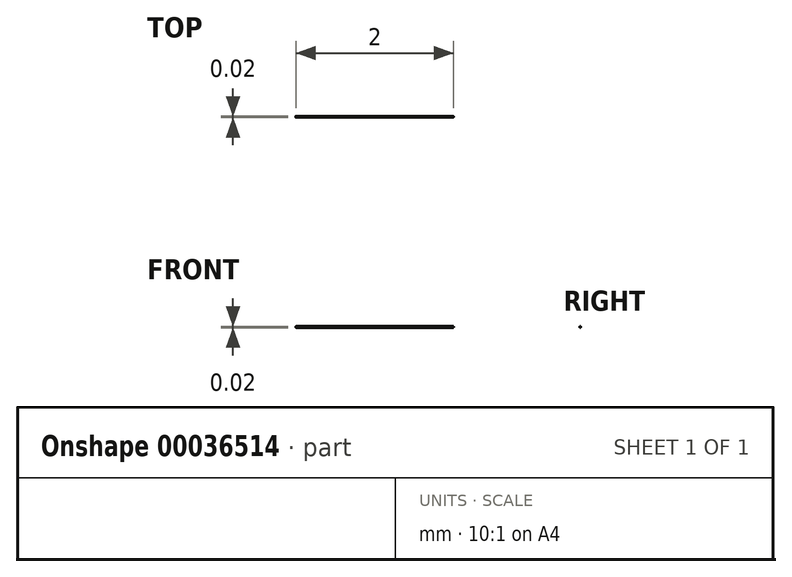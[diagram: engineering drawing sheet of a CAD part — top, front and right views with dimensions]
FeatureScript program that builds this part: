
annotation { "Feature Type Name" : "Feature", "Feature Type Description" : "" }
export const myFeature = defineFeature(function(context is Context, id is Id, definition is map)
    precondition{}
    {
        {
            var Q0;
            Q0=qCreatedBy(makeId("Right.planeOp"),FACE);
            var sketch = newSketch(context, id + "F0", { "sketchPlane" : qUnion([Q0])});
            skCircle(sketch, "E0", {"center": v(0, 0) * mm, "radius": 0 * mm});
            skSolve(sketch);
        }
        {
            var Q0;
            Q0=qSketchRegion(id+"F0",true);
            extrude(context, id + "F1", {"entities" : qUnion([Q0]), "depth" : 2 * mm, "offsetDistance" : 25 * mm});
        }
    });
